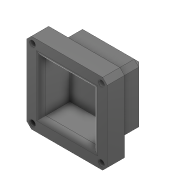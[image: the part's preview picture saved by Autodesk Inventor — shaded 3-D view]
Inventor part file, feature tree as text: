
AUTODESK INVENTOR PART (.ipt)
format: ipt  version: 2020.3 (Build 243373010, 373A)  size: 147,968 bytes
history: native  units: mm
features: extrude x3, sketch x3, fillet x2, chamfer x1, projected_geometry x1
ambient origin geometry x8: Origin, YZ Plane, XZ Plane, XY Plane, X Axis, Y Axis, Z Axis, Center Point
bodies: Solid1 (feature_tree)
feature tree (10):
  extrude  "Extrusion1"  Depth=4.25mm
  extrude  "Extrusion4"  Depth=12.5mm TaperAngle=0.0deg
  extrude  "Extrusion5"  Depth=12.5mm TaperAngle=0.0deg
  fillet  "Fillet2"  Radius=2.0mm
  chamfer  "Chamfer2"  Distance=2.0mm Angle=45.0deg
  fillet  "Fillet3"  Radius=2.0mm
  sketch  "Sketch1"  dims[d0=7.5mm d1=0.0mm d15=4.25mm]
  sketch  "Sketch4"  dims[d16=4.25mm d17=12.5mm d18=0.0mm]
  sketch  "Sketch5"  dims[d19=2.0mm d20=12.5mm d21=0.0mm d22=2.0mm d23=2.0mm d24=2.0mm d25=45.0deg d26=2.0mm]
  projected_geometry  "Projected Loop2"
